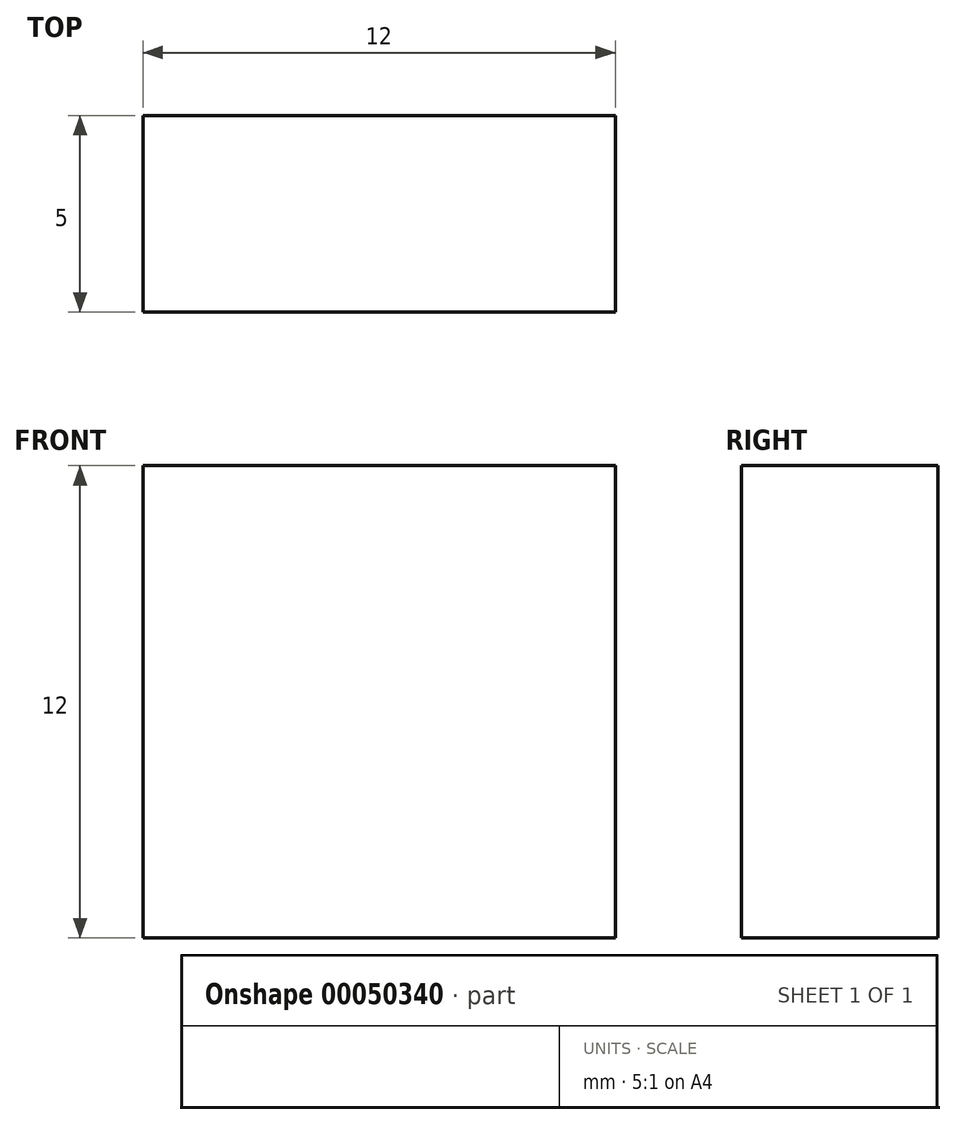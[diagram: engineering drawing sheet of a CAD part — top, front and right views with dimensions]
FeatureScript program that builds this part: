
annotation { "Feature Type Name" : "Feature", "Feature Type Description" : "" }
export const myFeature = defineFeature(function(context is Context, id is Id, definition is map)
    precondition{}
    {
        {
            var Q0;
            Q0=qCreatedBy(makeId("Front.planeOp"),FACE);
            var sketch = newSketch(context, id + "F0", { "sketchPlane" : qUnion([Q0])});
            skLineSegment(sketch, "E0.bottom", {"start": v(6, 6) * mm, "end": v(-6, 6) * mm});
            skLineSegment(sketch, "E0.top", {"start": v(6, -6) * mm, "end": v(-6, -6) * mm});
            skLineSegment(sketch, "E0.left", {"start": v(6, 6) * mm, "end": v(6, -6) * mm});
            skLineSegment(sketch, "E0.right", {"start": v(-6, 6) * mm, "end": v(-6, -6) * mm});
            skPoint(sketch, "E0.middle", {"position": v(0, 0) * mm});
            skSolve(sketch);
        }
        {
            var Q0;
            Q0=makeQuery(id+"F0.imprint","IMPRINT",FACE,{"disambiguationData":[TD([[makeQuery(id+"F0.imprint","IMPRINT",EDGE,{"derivedFrom":sQuery(id+"F0.wireOp",EDGE,"E0.bottom")}),1.0]])]});
            extrude(context, id + "F1", {"entities" : qUnion([Q0]), "depth" : 5 * mm});
        }
    });
